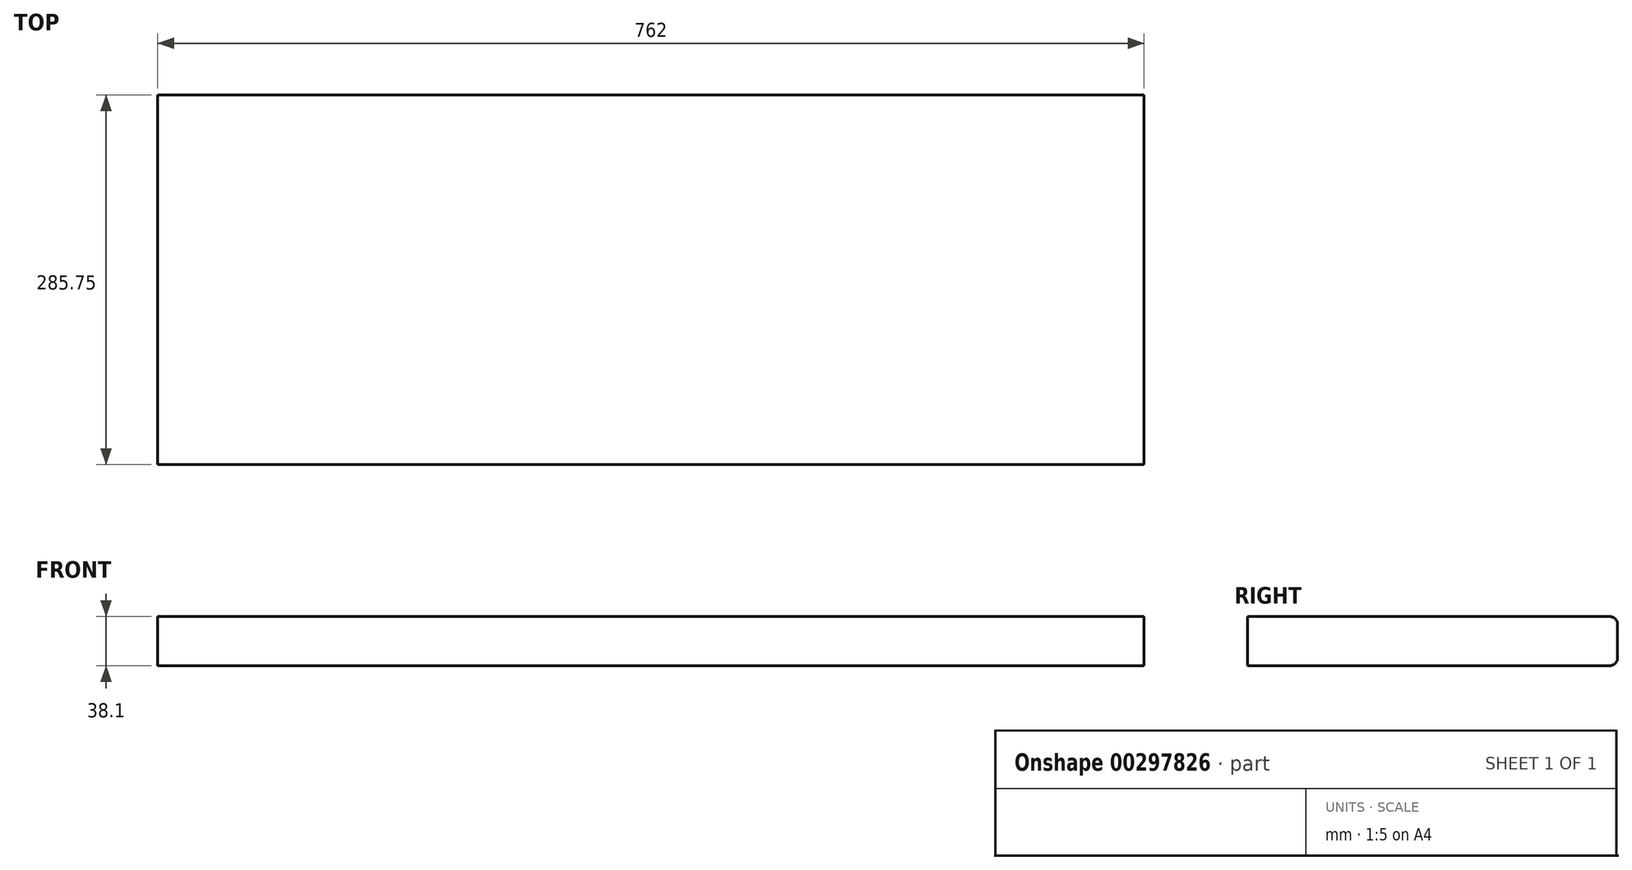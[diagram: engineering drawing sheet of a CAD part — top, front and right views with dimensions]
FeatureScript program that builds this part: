
annotation { "Feature Type Name" : "Feature", "Feature Type Description" : "" }
export const myFeature = defineFeature(function(context is Context, id is Id, definition is map)
    precondition{}
    {
        {
            var Q0;
            Q0=qCreatedBy(makeId("Top.planeOp"),FACE);
            var sketch = newSketch(context, id + "F0", { "sketchPlane" : qUnion([Q0])});
            skLineSegment(sketch, "E0.bottom", {"start": v(0, 0) * mm, "end": v(762, 0) * mm});
            skLineSegment(sketch, "E0.top", {"start": v(0, 285.75) * mm, "end": v(762, 285.75) * mm});
            skLineSegment(sketch, "E0.left", {"start": v(0, 0) * mm, "end": v(0, 285.75) * mm});
            skLineSegment(sketch, "E0.right", {"start": v(762, 0) * mm, "end": v(762, 285.75) * mm});
            skSolve(sketch);
        }
        {
            var Q0;
            Q0=makeQuery(id+"F0.imprint","IMPRINT",FACE,{"disambiguationData":[TD([[makeQuery(id+"F0.imprint","IMPRINT",EDGE,{"derivedFrom":sQuery(id+"F0.wireOp",EDGE,"E0.bottom")}),1.0]])]});
            extrude(context, id + "F1", {"entities" : qUnion([Q0]), "depth" : 38.1 * mm});
        }
        {
            var Q0;
            Q0=makeQuery(id+"F1.opExtrude","CAP_EDGE",EDGE,{"disambiguationData":[OSD([sQuery(id+"F0.wireOp",EDGE,"E0.top")])],"isStart":false});
            var Q1;
            Q1=makeQuery(id+"F1.opExtrude","CAP_EDGE",EDGE,{"disambiguationData":[OSD([sQuery(id+"F0.wireOp",EDGE,"E0.top")])],"isStart":true});
            fillet(context, id + "F2", {"entities" : qUnion([Q0, Q1]), "radius" : 6.35 * mm, "tangentPropagation" : true, "allowEdgeOverflow" : false});
        }
    });
